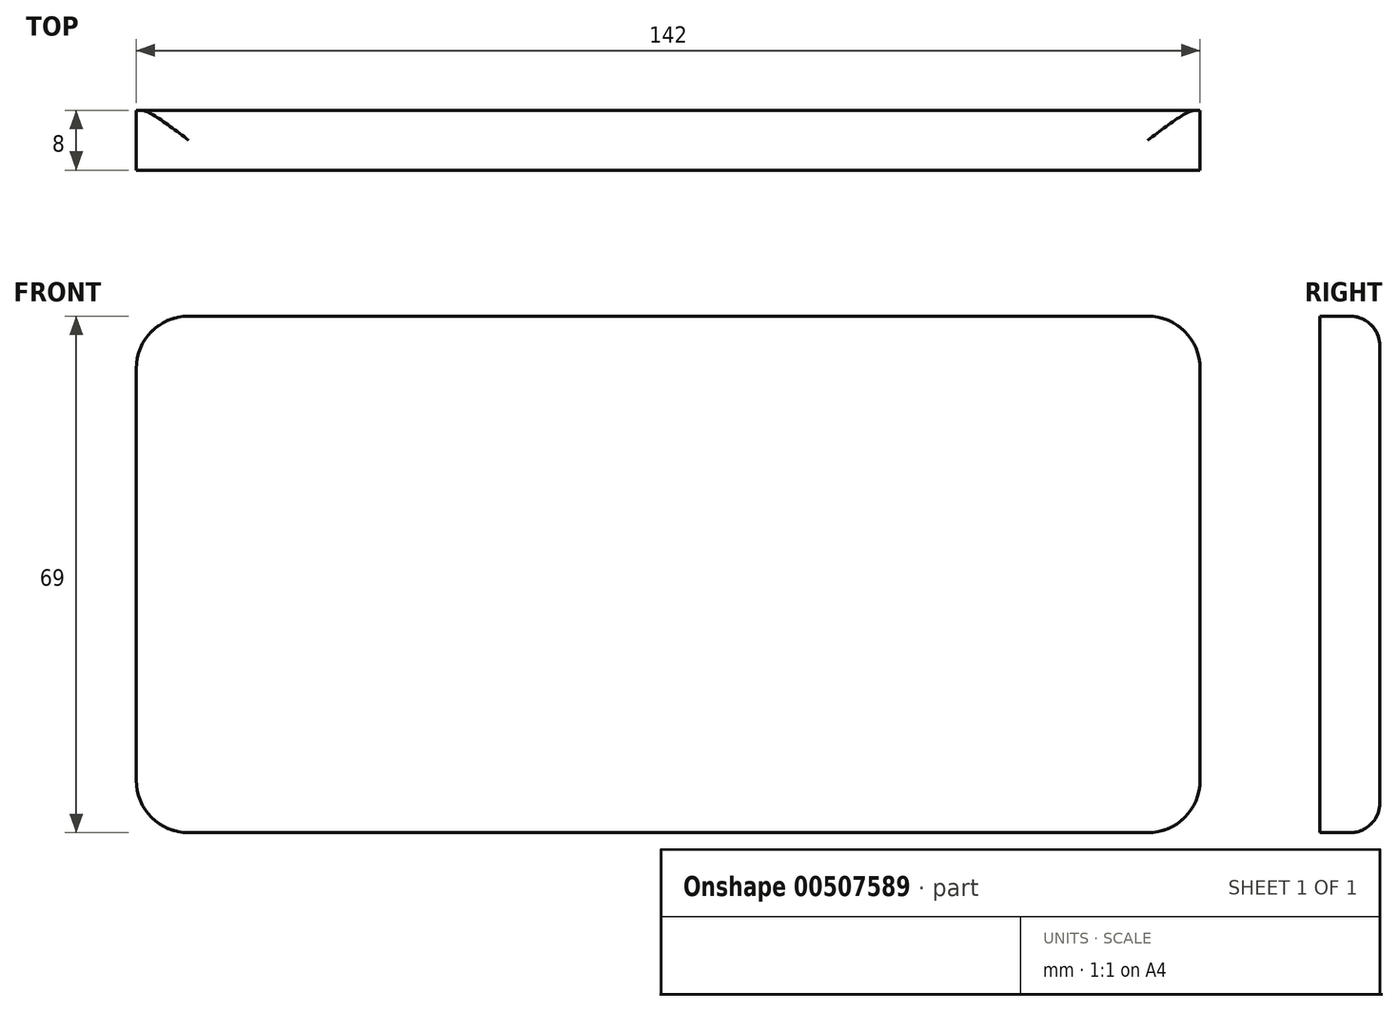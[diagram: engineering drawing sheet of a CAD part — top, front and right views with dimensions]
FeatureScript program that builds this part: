
annotation { "Feature Type Name" : "Feature", "Feature Type Description" : "" }
export const myFeature = defineFeature(function(context is Context, id is Id, definition is map)
    precondition{}
    {
        {
            var Q0;
            Q0=qCreatedBy(makeId("Front.planeOp"),FACE);
            var sketch = newSketch(context, id + "F0", { "sketchPlane" : qUnion([Q0])});
            skLineSegment(sketch, "E0.bottom", {"start": v(64, -34.5) * mm, "end": v(-64, -34.5) * mm});
            skLineSegment(sketch, "E0.top", {"start": v(64, 34.5) * mm, "end": v(-64, 34.5) * mm});
            skLineSegment(sketch, "E0.left", {"start": v(71, -27.5) * mm, "end": v(71, 27.5) * mm});
            skLineSegment(sketch, "E0.right", {"start": v(-71, -27.5) * mm, "end": v(-71, 27.5) * mm});
            skPoint(sketch, "E0.middle", {"position": v(0, 0) * mm});
            skPoint(sketch, "E1.visualSharp", {"position": v(71, 34.5) * mm});
            skArc(sketch, "E1.filletArc", {"start": v(71, 27.5) * mm, "mid": v(68.95, 32.45) * mm, "end": v(64, 34.5) * mm});
            skPoint(sketch, "E2.visualSharp", {"position": v(-71, 34.5) * mm});
            skArc(sketch, "E2.filletArc", {"start": v(-64, 34.5) * mm, "mid": v(-68.95, 32.45) * mm, "end": v(-71, 27.5) * mm});
            skPoint(sketch, "E3.visualSharp", {"position": v(-71, -34.5) * mm});
            skArc(sketch, "E3.filletArc", {"start": v(-71, -27.5) * mm, "mid": v(-68.95, -32.45) * mm, "end": v(-64, -34.5) * mm});
            skPoint(sketch, "E4.visualSharp", {"position": v(71, -34.5) * mm});
            skArc(sketch, "E4.filletArc", {"start": v(64, -34.5) * mm, "mid": v(68.95, -32.45) * mm, "end": v(71, -27.5) * mm});
            skSolve(sketch);
        }
        {
            var Q0;
            Q0=qSketchRegion(id+"F0",true);
            extrude(context, id + "F1", {"entities" : qUnion([Q0]), "depth" : 4 * mm, "hasSecondDirection" : true, "secondDirectionOppositeDirection" : true, "secondDirectionDepth" : 4 * mm});
        }
        {
            var Q0;
            Q0=makeQuery(id+"F1.opExtrude","CAP_EDGE",EDGE,{"disambiguationData":[OSD([sQuery(id+"F0.wireOp",EDGE,"E0.top")])],"isStart":true});
            var Q1;
            Q1=makeQuery(id+"F1.opExtrude","CAP_EDGE",EDGE,{"disambiguationData":[OSD([sQuery(id+"F0.wireOp",EDGE,"E0.bottom")])],"isStart":true});
            fillet(context, id + "F2", {"entities" : qUnion([Q0, Q1]), "radius" : 4 * mm, "allowEdgeOverflow" : false});
        }
    });
